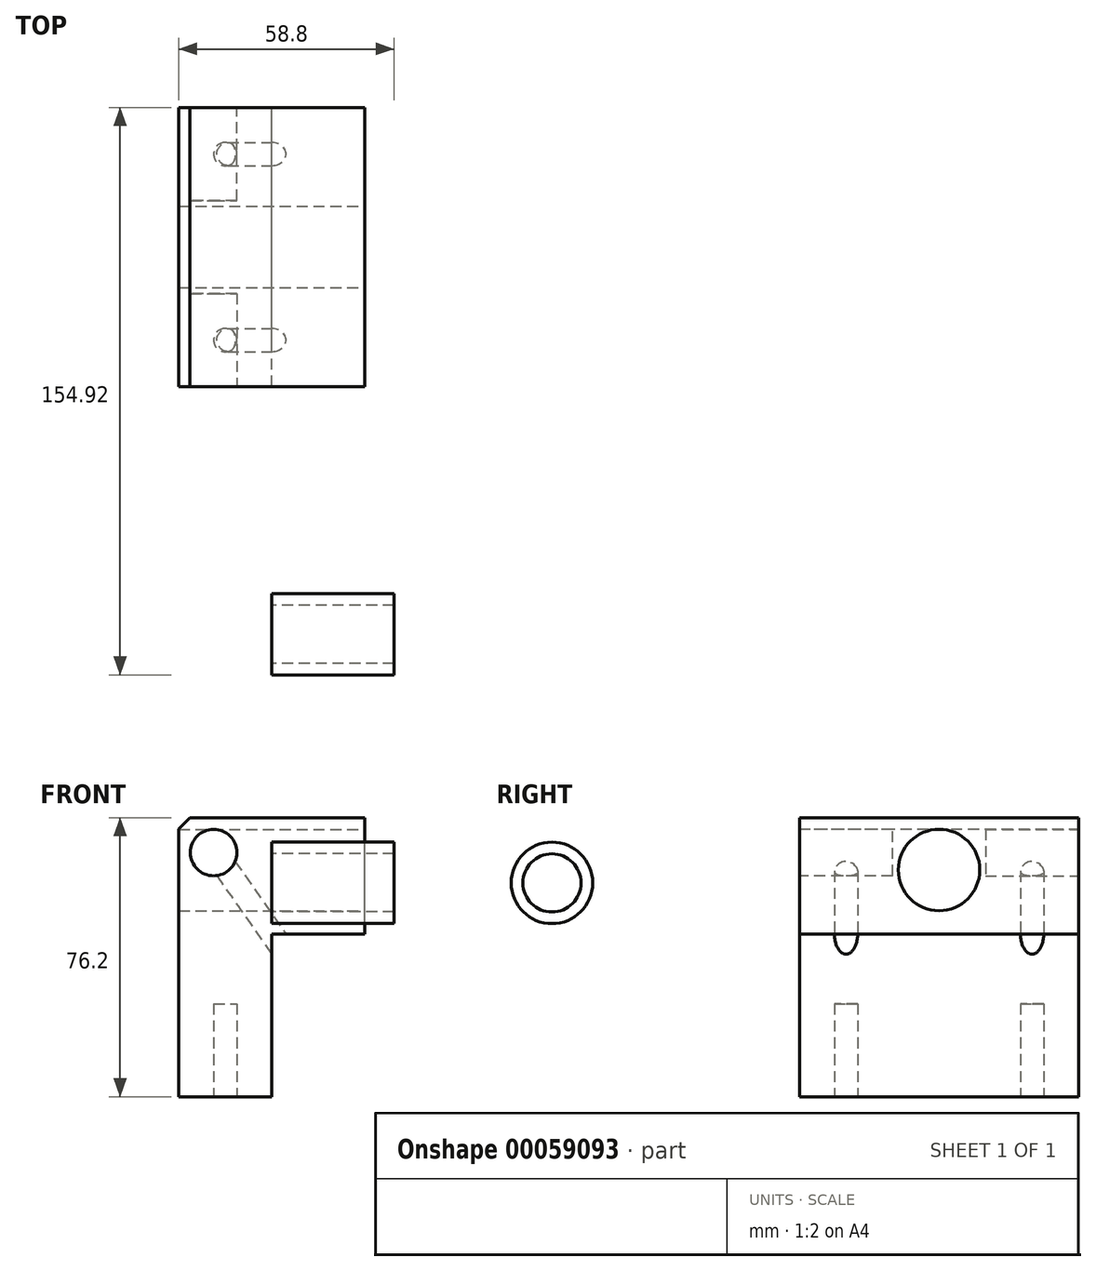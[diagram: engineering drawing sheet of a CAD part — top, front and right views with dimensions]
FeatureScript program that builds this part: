
annotation { "Feature Type Name" : "Feature", "Feature Type Description" : "" }
export const myFeature = defineFeature(function(context is Context, id is Id, definition is map)
    precondition{}
    {
        {
            var Q0;
            Q0=qCreatedBy(makeId("Front.planeOp"),FACE);
            var sketch = newSketch(context, id + "F0", { "sketchPlane" : qUnion([Q0])});
            skLineSegment(sketch, "E0.rect.bottom", {"start": v(0, -50.8) * mm, "end": v(-25.4, -50.8) * mm});
            skLineSegment(sketch, "E0.rect.top", {"start": v(25.4, 25.4) * mm, "end": v(-25.4, 25.4) * mm});
            skLineSegment(sketch, "E0.rect.left", {"start": v(25.4, -6.35) * mm, "end": v(25.4, 25.4) * mm});
            skLineSegment(sketch, "E0.rect.right", {"start": v(-25.4, -50.8) * mm, "end": v(-25.4, 25.4) * mm});
            skPoint(sketch, "E0.rect.middle", {"position": v(0, 0) * mm});
            skLineSegment(sketch, "E1", {"start": v(0, -6.35) * mm, "end": v(25.4, -6.35) * mm});
            skLineSegment(sketch, "E2", {"start": v(0, -6.35) * mm, "end": v(0, -50.8) * mm});
            skCircle(sketch, "E3", {"center": v(-15.88, 15.87) * mm, "radius": 6.35 * mm});
            skPoint(sketch, "E4.orphan", {"position": v(-25.4, -6.35) * mm});
            skSolve(sketch);
        }
        {
            var Q0;
            Q0=makeQuery(id+"F0.imprint","IMPRINT",FACE,{"disambiguationData":[TD([[makeQuery(id+"F0.imprint","IMPRINT",EDGE,{"derivedFrom":sQuery(id+"F0.wireOp",EDGE,"E0.rect.bottom")}),-1.0]])]});
            var Q1;
            Q1=makeQuery(id+"F0.imprint","IMPRINT",FACE,{"disambiguationData":[TD([[makeQuery(id+"F0.imprint","IMPRINT",EDGE,{"derivedFrom":sQuery(id+"F0.wireOp",EDGE,"E3")}),1.0]])]});
            extrude(context, id + "F1", {"entities" : qUnion([Q0, Q1]), "depth" : 76.2 * mm});
        }
        {
            var Q0;
            Q0=makeQuery(id+"F1.opExtrude","SWEPT_FACE",FACE,{"disambiguationData":[OSD([sQuery(id+"F0.wireOp",EDGE,"E0.rect.left")])]});
            var sketch = newSketch(context, id + "F2", { "sketchPlane" : qUnion([Q0])});
            skLineSegment(sketch, "E5", {"start": v(-76.2, 11.11) * mm, "end": v(0, 11.11) * mm, "construction": true});
            skLineSegment(sketch, "E6", {"start": v(-38.1, 25.4) * mm, "end": v(-38.1, -6.35) * mm, "construction": true});
            skCircle(sketch, "E7", {"center": v(-38.1, 11.11) * mm, "radius": 11.11 * mm});
            skSolve(sketch);
        }
        {
            var Q0;
            Q0=makeQuery(id+"F2.imprint","IMPRINT",FACE,{"disambiguationData":[TD([[makeQuery(id+"F2.imprint","IMPRINT",EDGE,{"derivedFrom":sQuery(id+"F2.wireOp",EDGE,"E7")}),1.0]])]});
            extrude(context, id + "F3", {"entities" : qUnion([Q0]), "operationType" : NewBodyOperationType.REMOVE, "endBound" : BoundingType.THROUGH_ALL, "oppositeDirection" : true, "depth" : 25.4 * mm});
        }
        {
            var Q0;
            Q0=makeQuery(id+"F1.opExtrude","CAP_FACE",FACE,{"disambiguationData":[OSD([sQuery(id+"F0.wireOp",EDGE,"E0.rect.bottom"),sQuery(id+"F0.wireOp",EDGE,"E0.rect.top"),sQuery(id+"F0.wireOp",EDGE,"E0.rect.left"),sQuery(id+"F0.wireOp",EDGE,"E0.rect.right"),sQuery(id+"F0.wireOp",EDGE,"E1"),sQuery(id+"F0.wireOp",EDGE,"E2")])],"isStart":false});
            var sketch = newSketch(context, id + "F4", { "sketchPlane" : qUnion([Q0])});
            skLineSegment(sketch, "E8", {"start": v(-25.4, 15.87) * mm, "end": v(25.4, 15.88) * mm, "construction": true});
            skLineSegment(sketch, "E9", {"start": v(-15.88, 25.4) * mm, "end": v(-15.87, 4.05) * mm, "construction": true});
            skCircle(sketch, "E10", {"center": v(-15.88, 15.87) * mm, "radius": 6.35 * mm});
            skSolve(sketch);
        }
        {
            var Q0;
            Q0=makeQuery(id+"F4.imprint","IMPRINT",FACE,{"disambiguationData":[TD([[makeQuery(id+"F4.imprint","IMPRINT",EDGE,{"derivedFrom":sQuery(id+"F4.wireOp",EDGE,"E10")}),1.0]])]});
            extrude(context, id + "F5", {"entities" : qUnion([Q0]), "operationType" : NewBodyOperationType.REMOVE, "oppositeDirection" : true, "depth" : 25.4 * mm});
        }
        {
            var Q0;
            Q0=makeQuery(id+"F1.opExtrude","CAP_FACE",FACE,{"disambiguationData":[OSD([sQuery(id+"F0.wireOp",EDGE,"E0.rect.bottom"),sQuery(id+"F0.wireOp",EDGE,"E0.rect.top"),sQuery(id+"F0.wireOp",EDGE,"E0.rect.left"),sQuery(id+"F0.wireOp",EDGE,"E0.rect.right"),sQuery(id+"F0.wireOp",EDGE,"E1"),sQuery(id+"F0.wireOp",EDGE,"E2")])],"isStart":true});
            var sketch = newSketch(context, id + "F6", { "sketchPlane" : qUnion([Q0])});
            skLineSegment(sketch, "E11", {"start": v(-25.4, 15.87) * mm, "end": v(25.4, 15.88) * mm, "construction": true});
            skLineSegment(sketch, "E12", {"start": v(15.87, 25.4) * mm, "end": v(15.88, 2.23) * mm, "construction": true});
            skCircle(sketch, "E13", {"center": v(15.88, 15.87) * mm, "radius": 6.35 * mm});
            skSolve(sketch);
        }
        {
            var Q0;
            Q0=makeQuery(id+"F6.imprint","IMPRINT",FACE,{"disambiguationData":[TD([[makeQuery(id+"F6.imprint","IMPRINT",EDGE,{"derivedFrom":sQuery(id+"F6.wireOp",EDGE,"E13")}),1.0]])]});
            extrude(context, id + "F7", {"entities" : qUnion([Q0]), "operationType" : NewBodyOperationType.REMOVE, "oppositeDirection" : true, "depth" : 25.4 * mm});
        }
        {
            var Q0;
            Q0=makeQuery(id+"F1.opExtrude","SWEPT_FACE",FACE,{"disambiguationData":[OSD([sQuery(id+"F0.wireOp",EDGE,"E0.rect.bottom")])]});
            var sketch = newSketch(context, id + "F8", { "sketchPlane" : qUnion([Q0])});
            skLineSegment(sketch, "E14", {"start": v(-12.7, 76.2) * mm, "end": v(-12.7, 0) * mm, "construction": true});
            skLineSegment(sketch, "E15", {"start": v(-25.4, 63.5) * mm, "end": v(0, 63.5) * mm, "construction": true});
            skLineSegment(sketch, "E16", {"start": v(-25.4, 12.7) * mm, "end": v(0, 12.7) * mm, "construction": true});
            skCircle(sketch, "E17", {"center": v(-12.7, 63.5) * mm, "radius": 3.18 * mm});
            skCircle(sketch, "E18", {"center": v(-12.7, 12.7) * mm, "radius": 3.18 * mm});
            skSolve(sketch);
        }
        {
            var Q0;
            Q0=makeQuery(id+"F8.imprint","IMPRINT",FACE,{"disambiguationData":[TD([[makeQuery(id+"F8.imprint","IMPRINT",EDGE,{"derivedFrom":sQuery(id+"F8.wireOp",EDGE,"E17")}),1.0]])]});
            var Q1;
            Q1=makeQuery(id+"F8.imprint","IMPRINT",FACE,{"disambiguationData":[TD([[makeQuery(id+"F8.imprint","IMPRINT",EDGE,{"derivedFrom":sQuery(id+"F8.wireOp",EDGE,"E18")}),1.0]])]});
            extrude(context, id + "F9", {"entities" : qUnion([Q0, Q1]), "operationType" : NewBodyOperationType.REMOVE, "oppositeDirection" : true, "depth" : 25.4 * mm});
        }
        {
            var Q0;
            Q0=makeQuery(id+"F1.opExtrude","SWEPT_EDGE",EDGE,{"disambiguationData":[OSD([sQuery(id+"F0.wireOp",EDGE,"E0.rect.top"),sQuery(id+"F0.wireOp",EDGE,"E0.rect.right")])]});
            chamfer(context, id + "F10", {"entities" : qUnion([Q0]), "width" : 3.05 * mm, "tangentPropagation" : true});
        }
        {
            var Q0;
            Q0=makeQuery(id+"F1.opExtrude","SWEPT_EDGE",EDGE,{"disambiguationData":[OSD([sQuery(id+"F0.wireOp",EDGE,"E1"),sQuery(id+"F0.wireOp",EDGE,"E2")])]});
            cPlane(context, id + "F11", {"entities" : qUnion([Q0]), "cplaneType" : CPlaneType.LINE_ANGLE, "offset" : 152.4 * mm, "angle" : 145 * degree, "flipAlignment" : true, "width" : 152.4 * mm, "height" : 152.4 * mm});
        }
        {
            var Q0;
            Q0=qCreatedBy(id+"F11.planeOp",FACE);
            var sketch = newSketch(context, id + "F12", { "sketchPlane" : qUnion([Q0])});
            skCircle(sketch, "E19", {"center": v(-3.64, 63.5) * mm, "radius": 3.18 * mm});
            skCircle(sketch, "E20", {"center": v(-3.64, 12.7) * mm, "radius": 3.18 * mm});
            skPoint(sketch, "E21.0.2.end.orphan", {"position": v(-3.64, 76.2) * mm});
            skPoint(sketch, "E21.0.1.end.orphan", {"position": v(17.16, 76.2) * mm});
            skPoint(sketch, "E21.0.0.end.orphan", {"position": v(17.16, 0) * mm});
            skPoint(sketch, "E21.0.0.start.orphan", {"position": v(-3.64, 0) * mm});
            skSolve(sketch);
        }
        {
            var Q0;
            Q0 = qSketchRegion(id + "F12", true);
            extrude(context, id + "F13", {"entities" : qUnion([Q0]), "operationType" : NewBodyOperationType.REMOVE, "oppositeDirection" : true, "depth" : 50.8 * mm, "symmetric" : true});
        }
        {
            var Q0;
            Q0=qCreatedBy(makeId("Right.planeOp"),FACE);
            var sketch = newSketch(context, id + "F14", { "sketchPlane" : qUnion([Q0])});
            skCircle(sketch, "E22", {"center": v(-143.8, 7.57) * mm, "radius": 7.94 * mm});
            skCircle(sketch, "E23", {"center": v(-143.8, 7.57) * mm, "radius": 11.11 * mm});
            skSolve(sketch);
        }
        {
            var Q0;
            Q0=makeQuery(id+"F14.imprint","IMPRINT",FACE,{"disambiguationData":[TD([[makeQuery(id+"F14.imprint","IMPRINT",EDGE,{"derivedFrom":sQuery(id+"F14.wireOp",EDGE,"E22")}),-1.0]])]});
            extrude(context, id + "F15", {"entities" : qUnion([Q0]), "depth" : 33.4 * mm});
        }
    });
